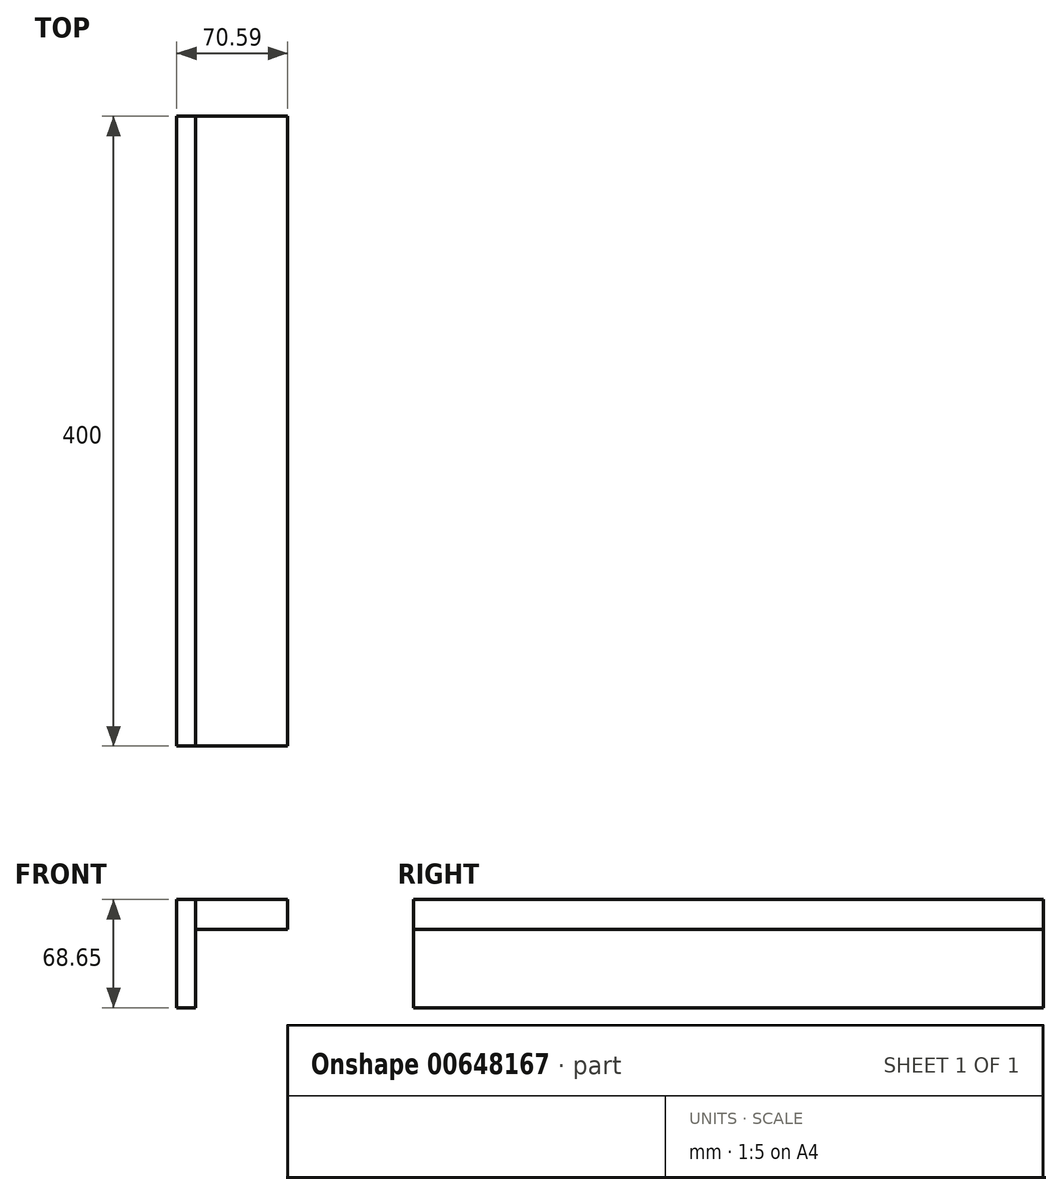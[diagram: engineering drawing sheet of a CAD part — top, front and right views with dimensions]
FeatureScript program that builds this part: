
annotation { "Feature Type Name" : "Feature", "Feature Type Description" : "" }
export const myFeature = defineFeature(function(context is Context, id is Id, definition is map)
    precondition{}
    {
        {
            var Q0;
            Q0=qCreatedBy(makeId("Front.planeOp"),FACE);
            var sketch = newSketch(context, id + "F0", { "sketchPlane" : qUnion([Q0])});
            skLineSegment(sketch, "E0.bottom", {"start": v(0, 0) * mm, "end": v(12.03, 0) * mm});
            skLineSegment(sketch, "E0.top", {"start": v(0, -68.65) * mm, "end": v(12.03, -68.65) * mm});
            skLineSegment(sketch, "E0.left", {"start": v(0, 0) * mm, "end": v(0, -68.65) * mm});
            skLineSegment(sketch, "E0.right", {"start": v(12.03, 0) * mm, "end": v(12.03, -68.65) * mm});
            skLineSegment(sketch, "E1.bottom", {"start": v(12.03, 0) * mm, "end": v(70.6, 0) * mm});
            skLineSegment(sketch, "E1.top", {"start": v(12.03, -19.08) * mm, "end": v(70.6, -19.08) * mm});
            skLineSegment(sketch, "E1.left", {"start": v(12.03, 0) * mm, "end": v(12.03, -19.08) * mm});
            skLineSegment(sketch, "E1.right", {"start": v(70.6, 0) * mm, "end": v(70.6, -19.08) * mm});
            skSolve(sketch);
        }
        {
            var Q0;
            Q0=makeQuery(id+"F0.imprint","IMPRINT",FACE,{"disambiguationData":[TD([[makeQuery(id+"F0.imprint","IMPRINT",EDGE,{"derivedFrom":sQuery(id+"F0.wireOp",EDGE,"E0.bottom")}),-1.0]])]});
            extrude(context, id + "F1", {"entities" : qUnion([Q0]), "depth" : 400 * mm, "offsetDistance" : 25 * mm});
        }
        {
            var Q0;
            Q0=makeQuery(id+"F0.imprint","IMPRINT",FACE,{"disambiguationData":[TD([[makeQuery(id+"F0.imprint","IMPRINT",EDGE,{"derivedFrom":sQuery(id+"F0.wireOp",EDGE,"E1.bottom")}),-1.0]])]});
            extrude(context, id + "F2", {"entities" : qUnion([Q0]), "depth" : 400 * mm, "offsetDistance" : 25 * mm});
        }
    });
